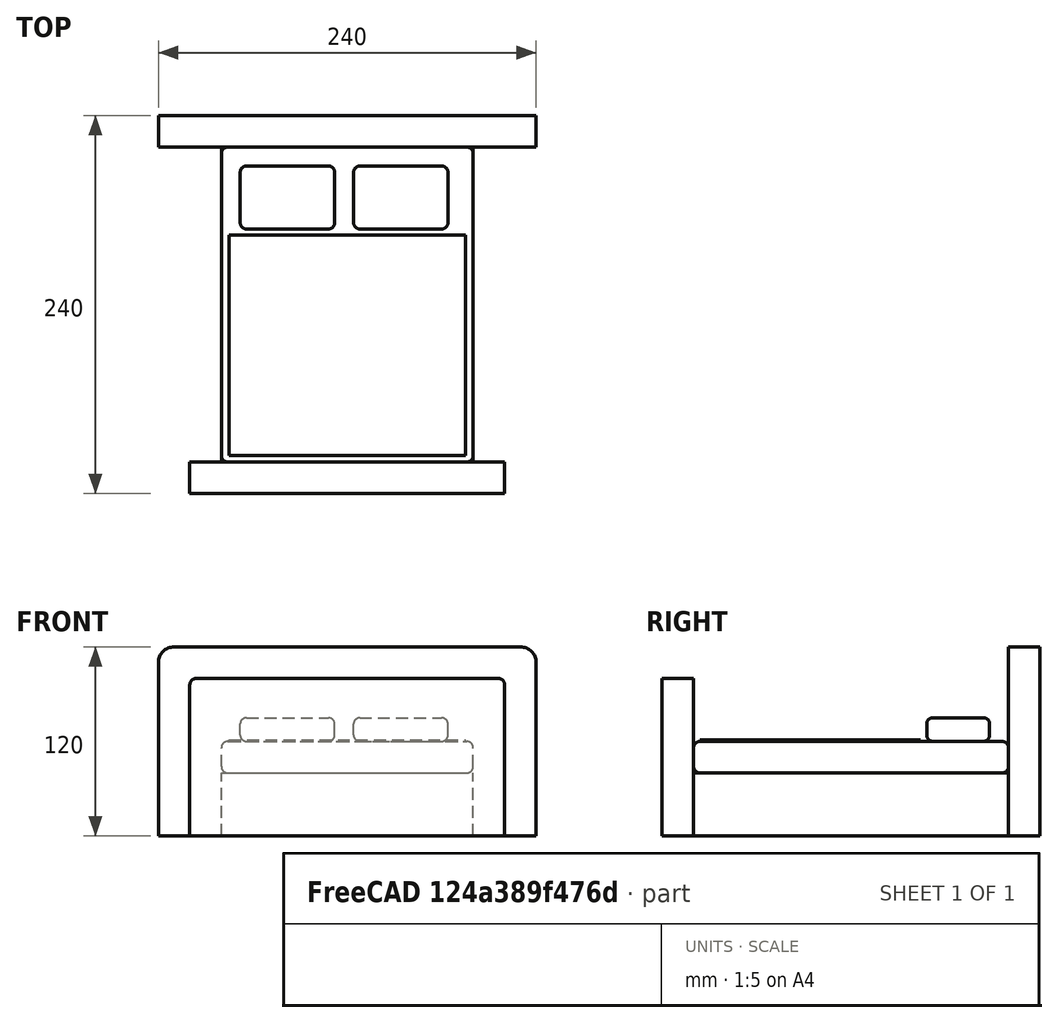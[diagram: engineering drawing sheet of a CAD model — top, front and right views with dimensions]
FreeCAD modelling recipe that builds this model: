
FCSTD DOCUMENT  (FreeCAD 0.21R33668 +26 (Git))
Label: Lit
License: All rights reserved
LicenseURL: http://en.wikipedia.org/wiki/All_rights_reserved
objects: Part::Box×7, Part::Fillet×5, Part::Compound×3
note: 15 computed .brp shape members not serialized (recipe doc carries the construction recipe); baked Part::Feature solids carry a one-line shape summary decoded from their .brp

FEATURE [Part::Box] Box  label="Sommier"
  AttacherType = Attacher::AttachEngine3D
  Height = 40
  Length = 160
  Width = 200
FEATURE [Part::Box] Box001  label="Cube001"
  AttacherType = Attacher::AttachEngine3D
  Height = 20
  Length = 160
  Placement = pos=(0,0,40) rot=(0,0,1;0rad)
  Width = 200
FEATURE [Part::Fillet] Fillet  label="Matelas"
  Base = -> Box001
  Edges = 12 edges r=4: [Edge1,Edge2,Edge3,Edge4,Edge5,Edge6,Edge7,Edge8,Edge9,Edge10,Edge11,Edge12]
FEATURE [Part::Box] Box002  label="Cube002"
  AttacherType = Attacher::AttachEngine3D
  Height = 120
  Length = 240
  Placement = pos=(-40,200,0) rot=(0,0,1;0rad)
  Width = 20
FEATURE [Part::Fillet] Fillet001  label="Tete de lit"
  Base = -> Box002
  Edges = 2 edges r=10: [Edge2,Edge6]
FEATURE [Part::Box] Box003  label="Cube003"
  AttacherType = Attacher::AttachEngine3D
  Height = 15
  Length = 60
  Placement = pos=(12,148,60) rot=(0,0,1;0rad)
  Width = 40
FEATURE [Part::Box] Box004  label="Cube004"
  AttacherType = Attacher::AttachEngine3D
  Height = 15
  Length = 60
  Placement = pos=(84,148,60) rot=(0,0,1;0rad)
  Width = 40
FEATURE [Part::Fillet] Fillet002
  Base = -> Box003
  Edges = 12 edges r=4: [Edge1,Edge2,Edge3,Edge4,Edge5,Edge6,Edge7,Edge8,Edge9,Edge10,Edge11,Edge12]
FEATURE [Part::Fillet] Fillet003
  Base = -> Box004
  Edges = 12 edges r=4: [Edge1,Edge2,Edge3,Edge4,Edge5,Edge6,Edge7,Edge8,Edge9,Edge10,Edge11,Edge12]
FEATURE [Part::Compound] Compound  label="Oreillers"
  Links = -> [Fillet003,Fillet002]
FEATURE [Part::Box] Box005  label="Cube005"
  AttacherType = Attacher::AttachEngine3D
  Height = 100
  Length = 200
  Placement = pos=(-20,-20,0) rot=(0,0,1;0rad)
  Width = 20
FEATURE [Part::Fillet] Fillet004  label="Pied de lit"
  Base = -> Box005
  Edges = 2 edges r=4: [Edge2,Edge6]
FEATURE [Part::Compound] Compound001  label="Lit"
  Links = -> [Fillet,Fillet001,Box,Fillet004]
FEATURE [Part::Box] Box006  label="Couverture"
  AttacherType = Attacher::AttachEngine3D
  Height = 1
  Length = 150
  Placement = pos=(5,4,60) rot=(0,0,50;0rad)
  Width = 140
FEATURE [Part::Compound] Compound002  label="Literie"
  Links = -> [Compound,Box006]
